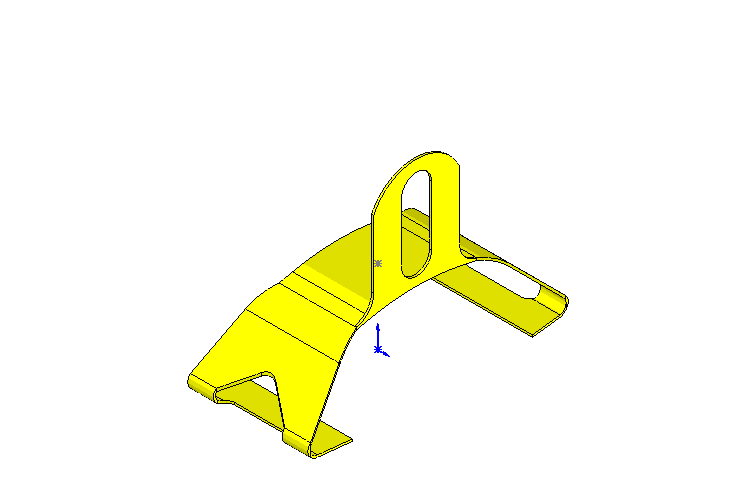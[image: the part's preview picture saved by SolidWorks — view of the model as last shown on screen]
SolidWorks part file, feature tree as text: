
SOLIDWORKS PART (.sldprt)
format: sldprt  version: not decoded by parser v0  size: 800,256 bytes
history: native  units: mm
features: sketch x7, plane x5, cut_extrude x4, extrude x2, material x1, fillet x1 (+10 scaffold rows collapsed)
feature tree (30):
  scaffold x10  (default folders/planes/origin — collapsed)
  material  "Matériau <non spécifié>"
  plane  "Plan de face"
  plane  "Plan de dessus"
  plane  "Plan de droite"
  sketch  "Esquisse1"  dims[c1.D5=0.1mm c1.D3=1.6mm c1.D8=~3.336064mm c1.D10=0.1mm c1.D4=50.0mm c2.D5=51.5mm c2.D6=10.0mm c2.D13=11.5mm c2.D8=1.6mm c2.D2=51.5mm c2.D3=51.5mm c2.D4=1.6mm c3.D6=11.5mm c3.D1=21.0mm c3.D2=33.0mm c3.D3=58.0mm c4.D6=2.5mm c4.D3=21.0mm c4.D7=33.0mm c4.D8=59.0mm c4.D11=3.0mm c4.D12=0.05mm c4.D2=370.0mm c4.D5=17.0mm c5.D8=59.7mm c5.D14=~338.322242mm c5.D3=371.5mm c5.D6=42.0mm c5.D5=17.0mm c5.D10=~39.282857mm c5.D11=~13.096332mm c5.D9=~23.05146mm c6.D3=~9.350811mm c7.D3=~90.225663deg c8.D3=~9.350811mm c9.D3=~90.225663deg c9.D5=~27.98646mm c9.D10=21.84mm c10.D5=~9.074285mm c10.D7=~3.02073mm c11.D5=21.84mm c11.D4=1.5mm c11.D9=1.5mm c11.D12=0.5mm]
  extrude  "Extrusion1"  Depth=30mm
  plane  "Plan1"  Offset=43mm
  plane  "Plan2"  Offset=1.6mm
  sketch  "Esquisse5"  dims[c1.D1=20.0mm c1.D2=11.0mm c1.D3=0.5mm c2.D2=8.5mm]
  extrude  "Extrusion2"  [1 undecoded]
  fillet  "Congé1"  Radius=5mm
  sketch  "Esquisse2"  dims[c1.D2=3.0mm c1.D4=3.0mm c1.D1=20.0mm c2.D2=20.0mm c2.D1=28.0mm c3.D2=1.0mm c3.D3=16.0mm c3.D4=50.0mm]
  cut_extrude  "Enlèv. mat.-Extru.1"  [1 undecoded]
  sketch  "Esquisse8"  dims[D2=2.0mm D1=3.0mm]
  cut_extrude  "Enlèv. mat.-Extru.2"  [1 undecoded]
  sketch  "Esquisse9"  dims[c1.D2=3.5mm c1.D3=11.0mm c1.D4=51.5mm c1.D1=7.0mm c2.D2=21.0mm c2.D4=2.0mm]
  cut_extrude  "Enlèv. mat.-Extru.4"  [1 undecoded]
  sketch  "Esquisse10"  dims[D1=11.0mm]
  cut_extrude  "Enlèv. mat.-Extru.5"  [1 undecoded]
  sketch  "Esquisse11"
decode coverage: 8 of 14 modeling features carry decoded parameters
note: ~ marks probable driven/reference dimensions
note: 5 parameter values undecoded
summary: no parameter record found for 5 features
note: suppression state not decoded; provenance and decode notes live in map.json
